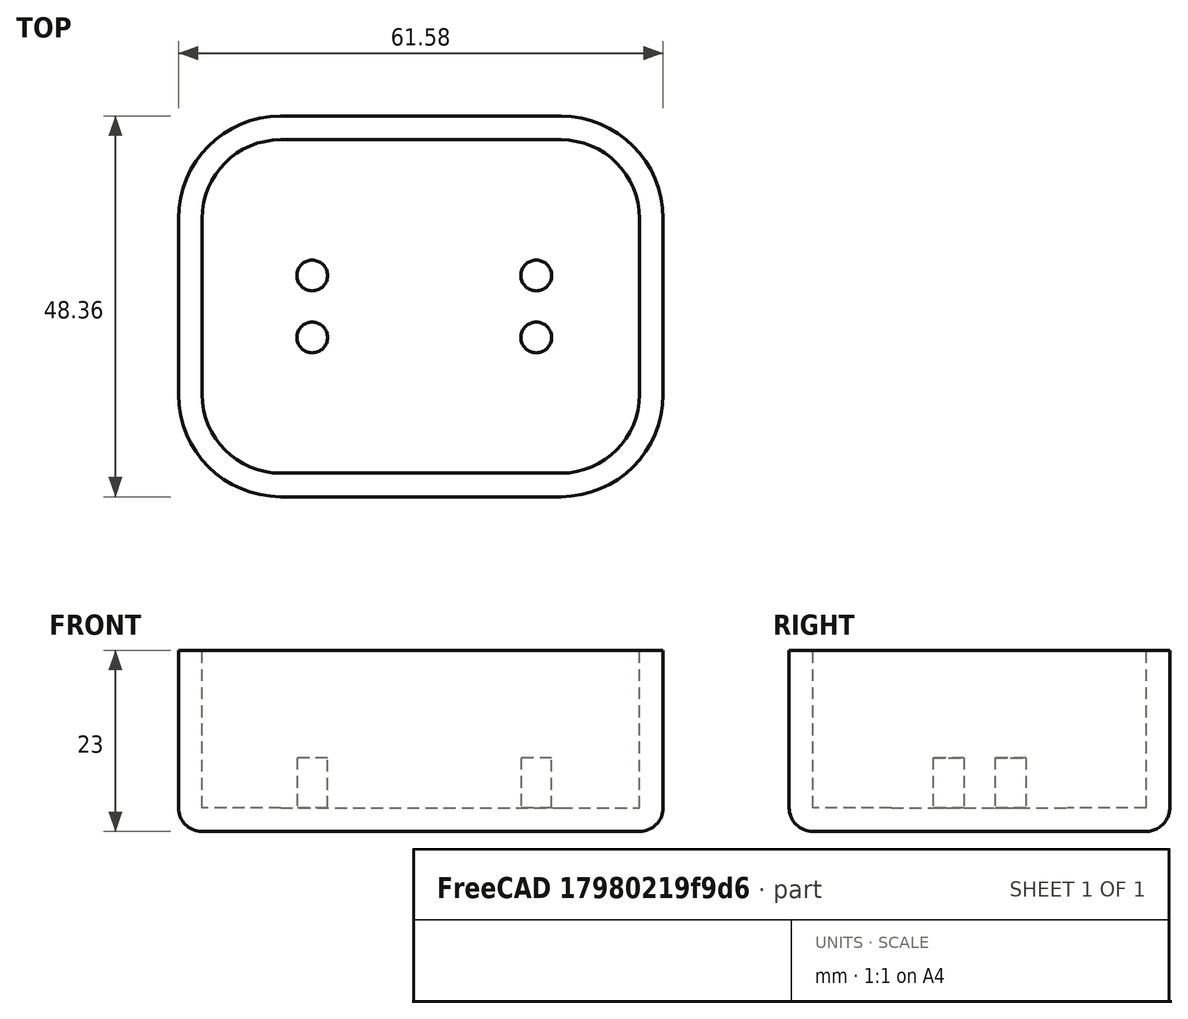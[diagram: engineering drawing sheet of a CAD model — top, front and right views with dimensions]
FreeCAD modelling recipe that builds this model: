
FCSTD DOCUMENT  (FreeCAD 0.21R33771 (Git))
Label: ElectricBox
License: All rights reserved
LicenseURL: http://en.wikipedia.org/wiki/All_rights_reserved
objects: Mesh::Feature×4, Sketcher::SketchObject×2, Part::Extrusion×2, App::Part×1, Spreadsheet::Sheet×1, Part::Thickness×1, Part::Fuse×1
note: 6 computed .brp shape members not serialized (recipe doc carries the construction recipe); baked Part::Feature solids carry a one-line shape summary decoded from their .brp

FEATURE [App::Part] Part
  Origin = -> Origin
FEATURE [Sketcher::SketchObject] Sketch  label="SketchBox"
  FullyConstrained = true
  MapMode = 2
  Support = -> [Part]
  expr: Constraints[19] = Spreadsheet.Clearance
  expr: Constraints[20] = Spreadsheet.SlotLength
  expr: Constraints[22] = Spreadsheet.AttachEndLen * 2 + (Spreadsheet.SlotWidth + Spreadsheet.SpacerWidth) * Spreadsheet.SlotNumber
  sketch-geometry (10):
    g0: ArcOfCircle CenterX=-17.79 CenterY=11.175 CenterZ=0 NormalX=0 NormalY=0 NormalZ=1 AngleXU=0 Radius=10 StartAngle=1.5708 EndAngle=3.14159
    g1: LineSegment StartX=-17.79 StartY=21.175 StartZ=0 EndX=17.79 EndY=21.175 EndZ=0
    g2: ArcOfCircle CenterX=17.79 CenterY=11.175 CenterZ=0 NormalX=0 NormalY=0 NormalZ=1 AngleXU=0 Radius=10 StartAngle=1e-16 EndAngle=1.5708
    g3: LineSegment StartX=27.79 StartY=11.175 StartZ=0 EndX=27.79 EndY=-11.175 EndZ=0
    g4: ArcOfCircle CenterX=17.79 CenterY=-11.175 CenterZ=0 NormalX=0 NormalY=0 NormalZ=1 AngleXU=0 Radius=10 StartAngle=4.71239 EndAngle=6.28319
    g5: LineSegment StartX=17.79 StartY=-21.175 StartZ=0 EndX=-17.79 EndY=-21.175 EndZ=0
    g6: ArcOfCircle CenterX=-17.79 CenterY=-11.175 CenterZ=0 NormalX=0 NormalY=0 NormalZ=1 AngleXU=0 Radius=10 StartAngle=3.14159 EndAngle=4.71239
    g7: LineSegment StartX=-27.79 StartY=-11.175 StartZ=0 EndX=-27.79 EndY=11.175 EndZ=0
    g8: GeomPoint X=-27.79 Y=21.175 Z=0
    g9: GeomPoint X=27.79 Y=-21.175 Z=0
  constraints (23):
    c: Tangent(g0,g1) = 1.5708
    c: Tangent(g1,g2) = 1.5708
    c: Tangent(g2,g3) = 1.5708
    c: Tangent(g3,g4) = 1.5708
    c: Tangent(g4,g5) = 1.5708
    c: Tangent(g5,g6) = 1.5708
    c: Tangent(g6,g7) = 1.5708
    c: Tangent(g7,g0) = 1.5708
    c: Horizontal(g1)
    c: Horizontal(g5)
    c: Vertical(g3)
    c: Vertical(g7)
    c: Equal(g0,g2)
    c: Equal(g2,g4)
    c: Equal(g4,g6)
    c: PointOnObject(g8,g1)
    c: PointOnObject(g8,g7)
    c: PointOnObject(g9,g3)
    c: PointOnObject(g9,g5)
    c: Radius(g0) = 10
    c: DistanceY(g7,g7) = 22.35
    c: Symmetric(g0,g4,g-1)
    c: DistanceX(g1,g1) = 35.58
FEATURE [Spreadsheet::Sheet] Spreadsheet
  cells = A1='SlotNumber; B1(SlotNumber)=2; A2='BaseLength; B2(BaseLength)=35.56; A3='HoleOffset; B3(HoleOffset)=3.56; A4='AttachEndLen; B4(AttachEndLen)=8.26; A5='SlotWidth; B5(SlotWidth)=7.62; A6='Clearance; B6(Clearance)=10; A7='AttachHoleDia; B7(AttachHoleDia)=4; A8='SlotLength; B8(SlotLength)=22.35; A9='SpacerWidth; B9(SpacerWidth)=1.91; A10='BodyDepth; B10(BodyDepth)=6.35; A11='Slot2Slot; B11(Slot2Slot)=9.53; A12='Hole2Hole; B12(Hole2Hole)=7.87
FEATURE [Part::Extrusion] Extrude
  Base = -> Sketch
  Dir = (0,0,1)
  DirMode = 2
  FaceMakerClass = Part::FaceMakerBullseye
  LengthFwd = 20
  LengthRev = 0
  Solid = true
  Symmetric = false
  expr: LengthFwd = 20 mm
FEATURE [Part::Thickness] Thickness
  Faces = -> Extrude [Face10]
  Intersection = false
  Join = 0
  Mode = 0
  SelfIntersection = false
  Value = 3
FEATURE [Sketcher::SketchObject] Sketch001  label="SketchPosts"
  ExternalGeometry = -> [Thickness]
  FullyConstrained = true
  MapMode = 5
  Support = -> [Thickness]
  expr: Constraints[0] = Spreadsheet.AttachHoleDia - 0.1
  expr: Constraints[2] = Spreadsheet.Hole2Hole
  expr: Constraints[5] = Spreadsheet.Hole2Hole
  expr: Constraints[6] = Spreadsheet.AttachHoleDia
  expr: Constraints[9] = Spreadsheet.Slot2Slot * Spreadsheet.SlotNumber + Spreadsheet.AttachEndLen * 2 - Spreadsheet.HoleOffset * 2
  sketch-geometry (4):
    g0: Circle CenterX=-13.79 CenterY=3.935 CenterZ=0 NormalX=0 NormalY=0 NormalZ=1 AngleXU=0 Radius=1.95
    g1: Circle CenterX=-13.79 CenterY=-3.935 CenterZ=0 NormalX=0 NormalY=0 NormalZ=1 AngleXU=0 Radius=1.95
    g2: Circle CenterX=14.67 CenterY=3.935 CenterZ=0 NormalX=0 NormalY=0 NormalZ=1 AngleXU=0 Radius=1.95
    g3: Circle CenterX=14.67 CenterY=-3.935 CenterZ=0 NormalX=0 NormalY=0 NormalZ=1 AngleXU=0 Radius=1.95
  constraints (10):
    c: Diameter(g0) = 3.9
    c: Equal(g0,g1)
    c: DistanceY(g1,g0) = 7.87
    c: Equal(g2,g3)
    c: Equal(g3,g0)
    c: DistanceY(g3,g2) = 7.87
    c: DistanceX(g-3,g0) = 4
    c: Symmetric(g1,g0,g-1)
    c: Symmetric(g2,g3,g-1)
    c: DistanceX(g1,g3) = 28.46
FEATURE [Part::Extrusion] Extrude001
  Base = -> Sketch001
  Dir = (0,0,1)
  DirMode = 2
  FaceMakerClass = Part::FaceMakerBullseye
  LengthFwd = 6.35
  LengthRev = 0
  Solid = true
  Symmetric = false
  expr: LengthFwd = Spreadsheet.BodyDepth
FEATURE [Part::Fuse] Fusion
  Base = -> Thickness
  Refine = true
  Tool = -> Extrude001
FEATURE [Mesh::Feature] Mesh  label="8Slot (Meshed)"
FEATURE [Mesh::Feature] Mesh001  label="6Slot (Meshed)"
FEATURE [Mesh::Feature] Mesh002  label="4Slot (Meshed)"
FEATURE [Mesh::Feature] Mesh003  label="2Slot (Meshed)"
